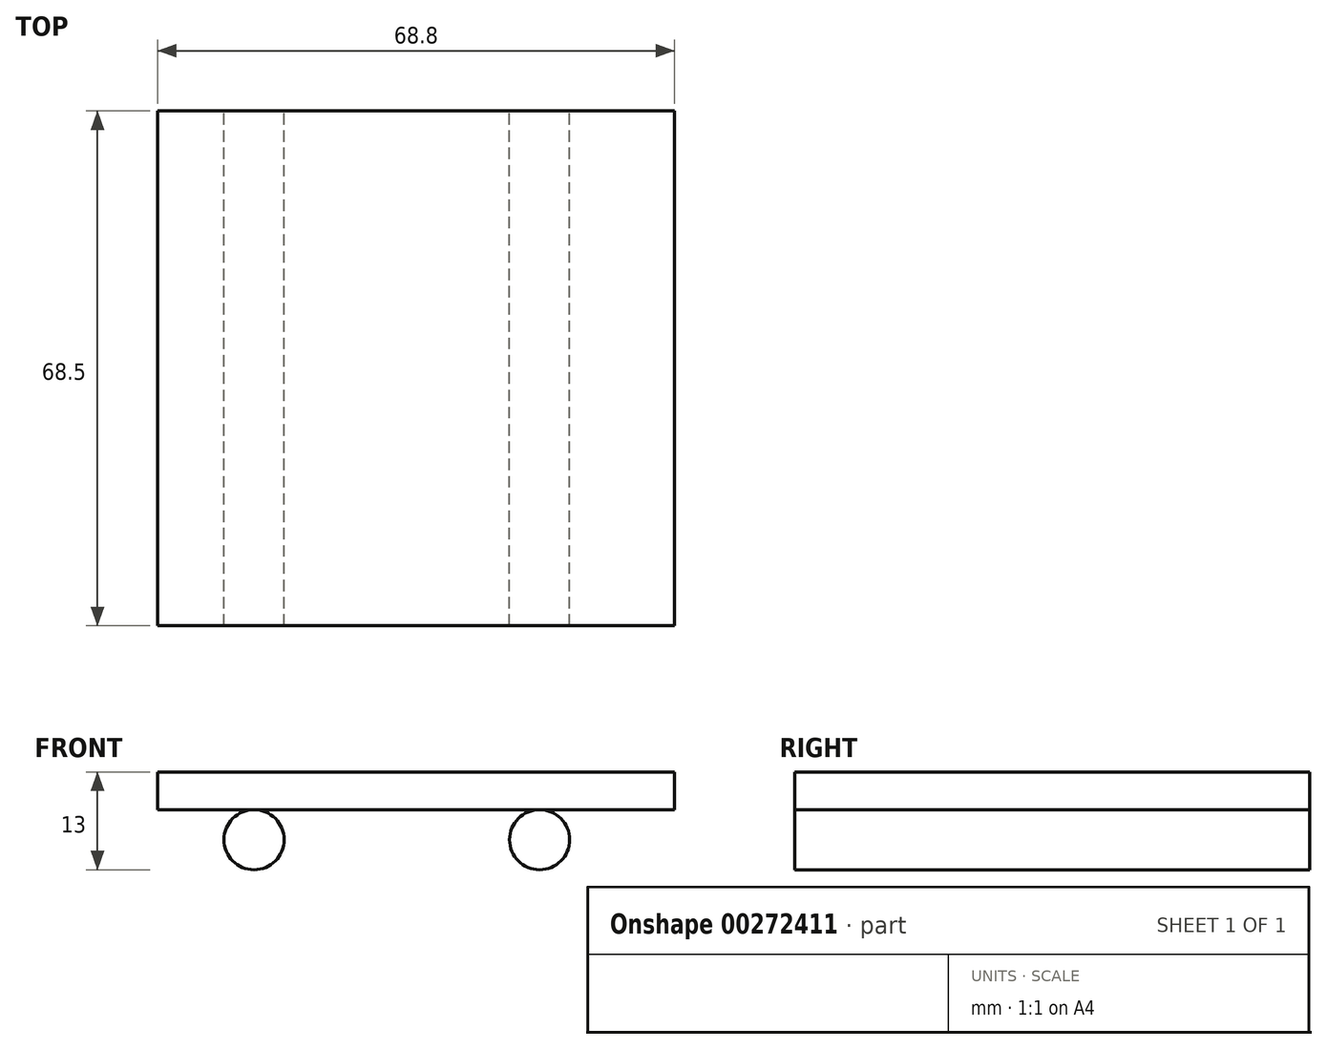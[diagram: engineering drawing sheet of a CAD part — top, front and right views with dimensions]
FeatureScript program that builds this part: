
annotation { "Feature Type Name" : "Feature", "Feature Type Description" : "" }
export const myFeature = defineFeature(function(context is Context, id is Id, definition is map)
    precondition{}
    {
        {
            var Q0;
            Q0=qCreatedBy(makeId("Front.planeOp"),FACE);
            var sketch = newSketch(context, id + "F0", { "sketchPlane" : qUnion([Q0])});
            skCircle(sketch, "E0", {"center": v(-33.48, 0) * mm, "radius": 4 * mm});
            skCircle(sketch, "E1", {"center": v(4.52, 0) * mm, "radius": 4 * mm});
            skLineSegment(sketch, "E2.bottom", {"start": v(22.5, 4) * mm, "end": v(-46.3, 4) * mm});
            skLineSegment(sketch, "E2.top", {"start": v(22.5, 9) * mm, "end": v(-46.3, 9) * mm});
            skLineSegment(sketch, "E2.left", {"start": v(22.5, 4) * mm, "end": v(22.5, 9) * mm});
            skLineSegment(sketch, "E2.right", {"start": v(-46.3, 4) * mm, "end": v(-46.3, 9) * mm});
            skPoint(sketch, "E2.middle", {"position": v(-11.9, 6.5) * mm});
            skSolve(sketch);
        }
        {
            var Q0;
            Q0 = qSketchRegion(id + "F0", true);
            extrude(context, id + "F1", {"entities" : qUnion([Q0]), "depth" : 68.5 * mm});
        }
    });
